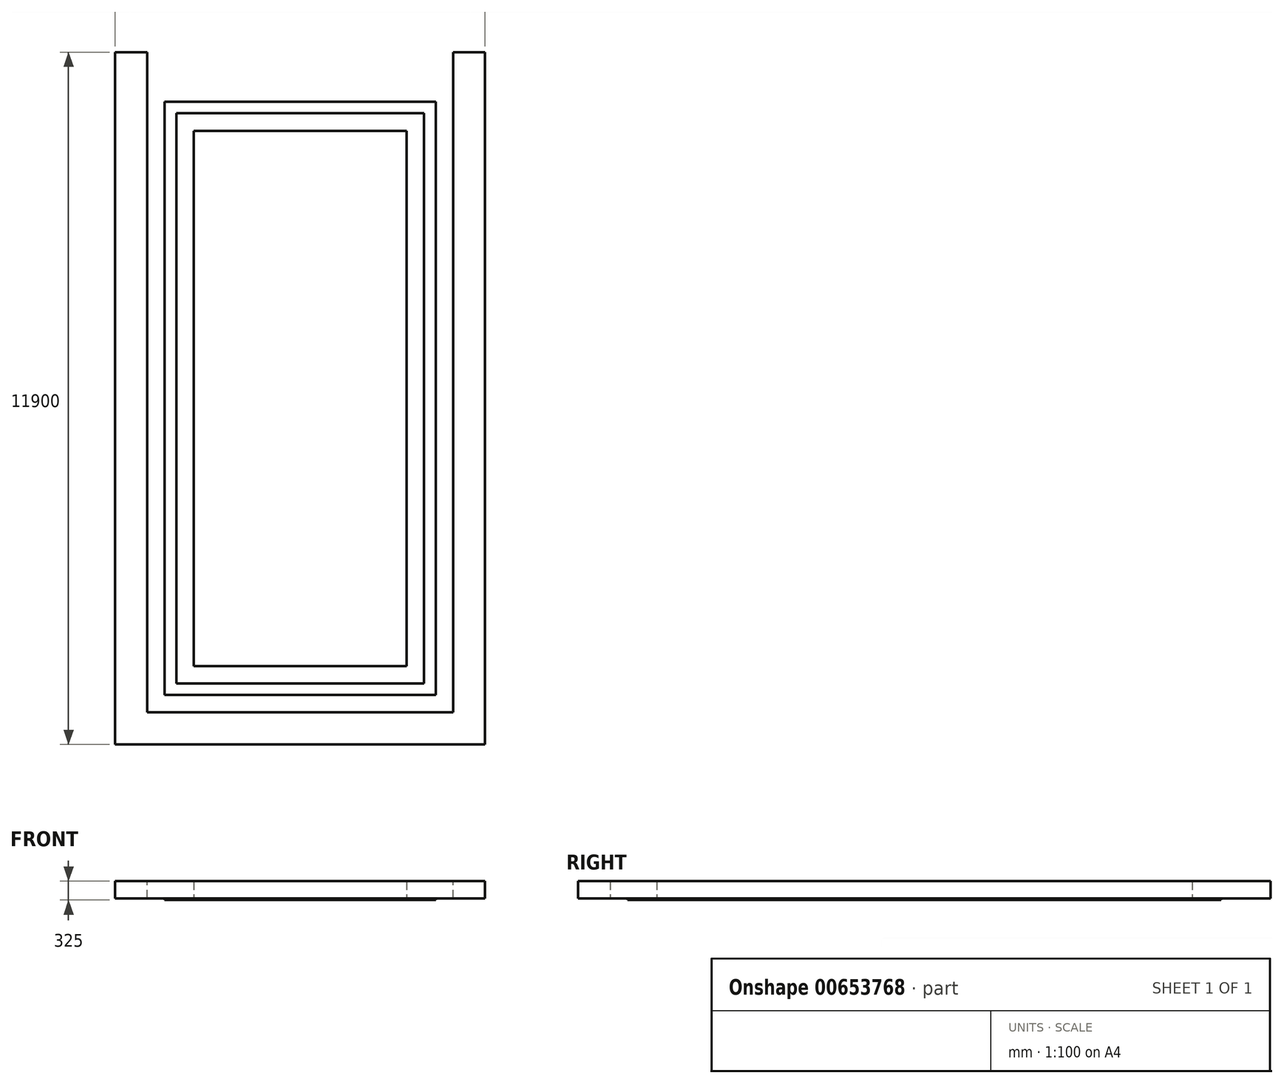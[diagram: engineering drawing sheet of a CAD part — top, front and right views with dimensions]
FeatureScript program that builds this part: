
annotation { "Feature Type Name" : "Feature", "Feature Type Description" : "" }
export const myFeature = defineFeature(function(context is Context, id is Id, definition is map)
    precondition{}
    {
        {
            var Q0;
            Q0=qCreatedBy(makeId("Top.planeOp"),FACE);
            var sketch = newSketch(context, id + "F0", { "sketchPlane" : qUnion([Q0])});
            skLineSegment(sketch, "E0.bottom", {"start": v(0, 0) * mm, "end": v(4256.34, 0) * mm});
            skLineSegment(sketch, "E0.top", {"start": v(0, 9800) * mm, "end": v(4256.34, 9800) * mm});
            skLineSegment(sketch, "E0.left", {"start": v(0, 0) * mm, "end": v(0, 9800) * mm});
            skLineSegment(sketch, "E0.right", {"start": v(4256.34, 0) * mm, "end": v(4256.34, 9800) * mm});
            skLineSegment(sketch, "E1.bottom", {"start": v(-200, -200) * mm, "end": v(4456.34, -200) * mm});
            skLineSegment(sketch, "E1.top", {"start": v(-200, 10000) * mm, "end": v(4456.34, 10000) * mm});
            skLineSegment(sketch, "E1.left", {"start": v(-200, -200) * mm, "end": v(-200, 10000) * mm});
            skLineSegment(sketch, "E1.right", {"start": v(4456.34, -200) * mm, "end": v(4456.34, 10000) * mm});
            skLineSegment(sketch, "E2.bottom", {"start": v(-500, -500) * mm, "end": v(4756.34, -500) * mm});
            skLineSegment(sketch, "E2.top", {"start": v(-500, 10300) * mm, "end": v(4756.34, 10300) * mm});
            skLineSegment(sketch, "E2.left", {"start": v(-500, -500) * mm, "end": v(-500, 10300) * mm});
            skLineSegment(sketch, "E2.right", {"start": v(4756.34, -500) * mm, "end": v(4756.34, 10300) * mm});
            skLineSegment(sketch, "E3.bottom", {"start": v(300, 300) * mm, "end": v(3956.34, 300) * mm});
            skLineSegment(sketch, "E3.top", {"start": v(300, 9500) * mm, "end": v(3956.34, 9500) * mm});
            skLineSegment(sketch, "E3.left", {"start": v(300, 300) * mm, "end": v(300, 9500) * mm});
            skLineSegment(sketch, "E3.right", {"start": v(3956.34, 300) * mm, "end": v(3956.34, 9500) * mm});
            skSolve(sketch);
        }
        {
            var Q0;
            Q0=makeQuery(id+"F0.imprint","IMPRINT",FACE,{"disambiguationData":[TD([[makeQuery(id+"F0.imprint","IMPRINT",EDGE,{"derivedFrom":sQuery(id+"F0.wireOp",EDGE,"E3.bottom")}),1.0]])]});
            extrude(context, id + "F1", {"entities" : qUnion([Q0]), "depth" : 300 * mm, "offsetDistance" : 25 * mm});
        }
        {
            var Q0;
            Q0=makeQuery(id+"F0.imprint","IMPRINT",FACE,{"disambiguationData":[TD([[makeQuery(id+"F0.imprint","IMPRINT",EDGE,{"derivedFrom":sQuery(id+"F0.wireOp",EDGE,"E3.bottom")}),1.0]])]});
            var sketch = newSketch(context, id + "F2", { "sketchPlane" : qUnion([Q0])});
            skLineSegment(sketch, "E4.0", {"start": v(-500, -500) * mm, "end": v(4756.34, -500) * mm});
            skLineSegment(sketch, "E5.0", {"start": v(-500, -500) * mm, "end": v(-500, 10300) * mm});
            skLineSegment(sketch, "E6.0", {"start": v(-500, 10300) * mm, "end": v(4756.34, 10300) * mm});
            skLineSegment(sketch, "E7.0", {"start": v(4756.34, -500) * mm, "end": v(4756.34, 10300) * mm});
            skLineSegment(sketch, "E8.bottom", {"start": v(-1050, 10850) * mm, "end": v(5306.34, 10850) * mm});
            skLineSegment(sketch, "E8.top", {"start": v(-1050, -1050) * mm, "end": v(5306.34, -1050) * mm});
            skLineSegment(sketch, "E8.left", {"start": v(-1050, 10850) * mm, "end": v(-1050, -1050) * mm});
            skLineSegment(sketch, "E8.right", {"start": v(5306.34, 10850) * mm, "end": v(5306.34, -1050) * mm});
            skSolve(sketch);
        }
        {
            var Q0;
            Q0=makeQuery(id+"F2.imprint","IMPRINT",FACE,{"disambiguationData":[TD([[makeQuery(id+"F2.imprint","IMPRINT",EDGE,{"derivedFrom":sQuery(id+"F2.wireOp",EDGE,"E4.0")}),-1.0]])]});
            extrude(context, id + "F3", {"entities" : qUnion([Q0]), "depth" : 300 * mm, "offsetDistance" : 25 * mm});
        }
        {
            var Q0;
            Q0=makeQuery(id+"F0.imprint","IMPRINT",FACE,{"disambiguationData":[TD([[makeQuery(id+"F0.imprint","IMPRINT",EDGE,{"derivedFrom":sQuery(id+"F0.wireOp",EDGE,"E0.bottom")}),-1.0]])]});
            extrude(context, id + "F4", {"entities" : qUnion([Q0]), "oppositeDirection" : true, "depth" : 25 * mm, "offsetDistance" : 25 * mm});
        }
        {
            var Q0;
            Q0=makeQuery(id+"F3.opExtrude","SWEPT_FACE",FACE,{"disambiguationData":[OSD([sQuery(id+"F2.wireOp",EDGE,"E6.0")])]});
            var sketch = newSketch(context, id + "F5", { "sketchPlane" : qUnion([Q0])});
            skLineSegment(sketch, "E9.0.0", {"start": v(-500, 0) * mm, "end": v(4756.34, 0) * mm});
            skLineSegment(sketch, "E9.0.1", {"start": v(4756.34, 0) * mm, "end": v(4756.34, 300) * mm});
            skLineSegment(sketch, "E9.0.2", {"start": v(4756.34, 300) * mm, "end": v(-500, 300) * mm});
            skLineSegment(sketch, "E9.0.3", {"start": v(-500, 300) * mm, "end": v(-500, 0) * mm});
            skSolve(sketch);
        }
        {
            var Q0;
            Q0=makeQuery(id+"F5.imprint","IMPRINT",FACE,{"disambiguationData":[TD([[makeQuery(id+"F5.imprint","IMPRINT",EDGE,{"derivedFrom":sQuery(id+"F5.wireOp",EDGE,"E9.0.0")}),1.0]])]});
            extrude(context, id + "F6", {"entities" : qUnion([Q0]), "operationType" : NewBodyOperationType.REMOVE, "endBound" : BoundingType.THROUGH_ALL, "oppositeDirection" : true, "depth" : 25 * mm, "offsetDistance" : 25 * mm});
        }
    });
